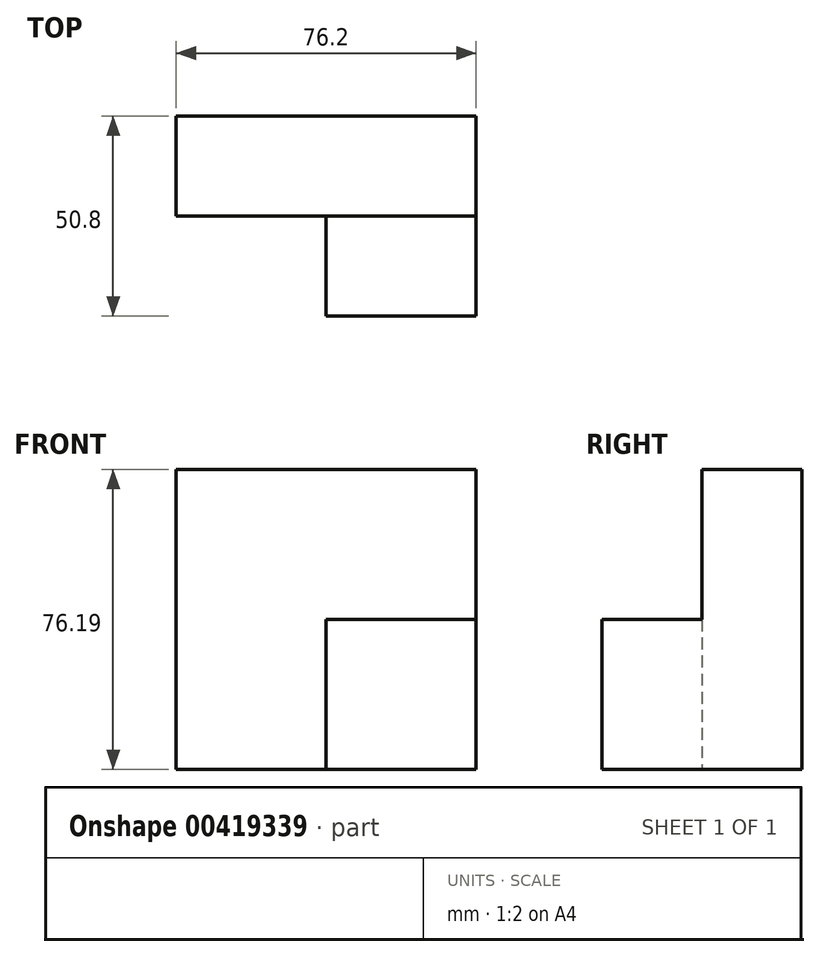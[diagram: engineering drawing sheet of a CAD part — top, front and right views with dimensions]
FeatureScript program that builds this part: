
annotation { "Feature Type Name" : "Feature", "Feature Type Description" : "" }
export const myFeature = defineFeature(function(context is Context, id is Id, definition is map)
    precondition{}
    {
        {
            var Q0;
            Q0=qCreatedBy(makeId("Front.planeOp"),FACE);
            var sketch = newSketch(context, id + "F0", { "sketchPlane" : qUnion([Q0])});
            skLineSegment(sketch, "E0", {"start": v(0, 0) * mm, "end": v(-76.2, 0) * mm});
            skLineSegment(sketch, "E1", {"start": v(-76.2, 0) * mm, "end": v(-76.2, 76.2) * mm});
            skLineSegment(sketch, "E2", {"start": v(-76.2, 76.2) * mm, "end": v(0, 76.2) * mm});
            skLineSegment(sketch, "E3", {"start": v(0, 76.2) * mm, "end": v(0, 0) * mm});
            skSolve(sketch);
        }
        {
            var Q0;
            Q0 = qSketchRegion(id + "F0", true);
            extrude(context, id + "F1", {"entities" : qUnion([Q0]), "depth" : 25.4 * mm});
        }
        {
            var Q0;
            Q0=qCreatedBy(makeId("Front.planeOp"),FACE);
            var sketch = newSketch(context, id + "F2", { "sketchPlane" : qUnion([Q0])});
            skLineSegment(sketch, "E4", {"start": v(0, 0) * mm, "end": v(-38.1, 0) * mm});
            skLineSegment(sketch, "E5", {"start": v(-38.1, 0) * mm, "end": v(-38.1, 38.1) * mm});
            skLineSegment(sketch, "E6", {"start": v(-38.1, 38.1) * mm, "end": v(0, 38.1) * mm});
            skLineSegment(sketch, "E7", {"start": v(0, 38.1) * mm, "end": v(0, 0) * mm});
            skSolve(sketch);
        }
        {
            var Q0;
            Q0 = qSketchRegion(id + "F2", true);
            extrude(context, id + "F3", {"entities" : qUnion([Q0]), "operationType" : NewBodyOperationType.ADD, "depth" : 50.8 * mm});
        }
    });
